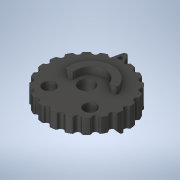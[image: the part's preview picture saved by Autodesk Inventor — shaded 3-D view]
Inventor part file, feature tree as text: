
AUTODESK INVENTOR PART (.ipt)
format: ipt  version: 2020.1 (Build 241239000, 239)  size: 398,848 bytes
history: native  units: mm
features: extrude x8, sketch x4, fillet x1, chamfer x1
ambient origin geometry x8: Origin, YZ Plane, XZ Plane, XY Plane, X Axis, Y Axis, Z Axis, Center Point
bodies: Solid1 (feature_tree)
feature tree (14):
  extrude  "Extrusion1"  Depth=1.25mm
  fillet  "Fillet1"  Radius=8.0mm
  sketch  "Sketch2"  dims[d10=6.3mm d11=12.0mm]
  extrude  "Extrusion2"  Depth=12.0mm
  extrude  "Extrusion3"  Depth=2.0mm TaperAngle=0.0deg
  chamfer  "Chamfer1"  Distance=2.0mm
  extrude  "Extrusion4"  TaperAngle=15.0deg  [1 undecoded]
  extrude  "Extrusion5"  Depth=3.0mm
  extrude  "Extrusion6"  Depth=3.0mm
  extrude  "Extrusion7"  Depth=3.0mm
  extrude  "Extrusion8"  Depth=3.0mm
  sketch  "Sketch1"  dims[d1=200.0mm d2=31.0mm d3=360.0deg d6=1.25mm d7=1.25mm d8=8.0mm d9=0.0mm]
  sketch  "Sketch4"  dims[d12=7.0mm d14=2.0mm d15=0.0mm d16=2.0mm d17=0.0mm]
  sketch  "Sketch5"  dims[d18=0.5mm d19=15.0deg d22=5.1mm d23=5.1mm d25=8.726646mm d26=1.5mm d27=9.0mm d28=6.0mm d29=7.330383mm d30=11.5mm d31=11.0mm d32=1.0mm d33=1.5mm d34=1.5mm d35=3.0mm d36=0.0mm d37=5.0mm d38=0.0mm d39=5.0mm d40=0.0mm d41=9.599311mm d43=180.0deg d44=0.0mm d45=2.0mm d46=2.0mm d47=45.0deg d48=1.0mm d49=3.0mm d50=0.0mm d51=0.4mm d52=10.0mm d53=0.0mm d54=0.7mm d55=3.0mm d56=0.0mm]
note: 1 required parameter value undecoded (feature->parameter linkage not recoverable at this tier; creation-order binding heuristic only, values carry confidence <= 0.55)
